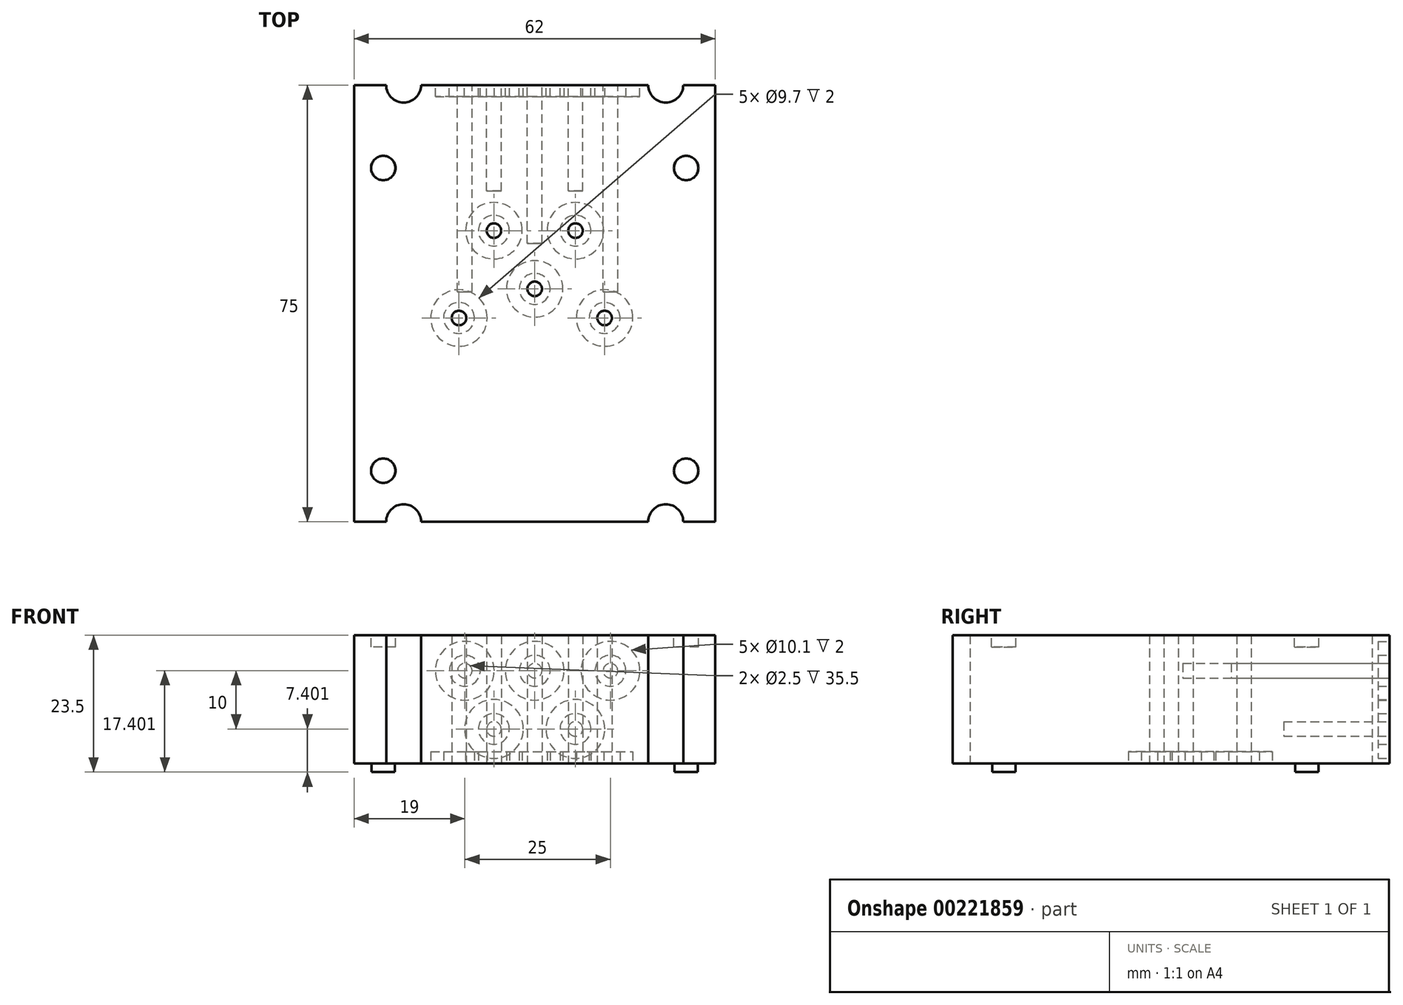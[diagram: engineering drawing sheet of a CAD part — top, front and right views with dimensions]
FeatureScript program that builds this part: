
annotation { "Feature Type Name" : "Feature", "Feature Type Description" : "" }
export const myFeature = defineFeature(function(context is Context, id is Id, definition is map)
    precondition{}
    {
        {
            var Q0;
            Q0=qCreatedBy(makeId("Top.planeOp"),FACE);
            var sketch = newSketch(context, id + "F0", { "sketchPlane" : qUnion([Q0])});
            skLineSegment(sketch, "E0.bottom", {"start": v(-31, 37.5) * mm, "end": v(31, 37.5) * mm});
            skLineSegment(sketch, "E0.top", {"start": v(-31, -37.5) * mm, "end": v(31, -37.5) * mm});
            skLineSegment(sketch, "E0.left", {"start": v(-31, 37.5) * mm, "end": v(-31, -37.5) * mm});
            skLineSegment(sketch, "E0.right", {"start": v(31, 37.5) * mm, "end": v(31, -37.5) * mm});
            skPoint(sketch, "E0.middle", {"position": v(0, 0) * mm});
            skSolve(sketch);
        }
        {
            var Q0;
            Q0=makeQuery(id+"F0.imprint","IMPRINT",FACE,{"disambiguationData":[TD([[makeQuery(id+"F0.imprint","IMPRINT",EDGE,{"derivedFrom":sQuery(id+"F0.wireOp",EDGE,"E0.bottom")}),-1.0]])]});
            extrude(context, id + "F1", {"entities" : qUnion([Q0]), "depth" : 14 * mm});
        }
        {
            var Q0;
            Q0=makeQuery(id+"F1.opExtrude","CAP_FACE",FACE,{"disambiguationData":[OSD([sQuery(id+"F0.wireOp",EDGE,"E0.bottom"),sQuery(id+"F0.wireOp",EDGE,"E0.top"),sQuery(id+"F0.wireOp",EDGE,"E0.left"),sQuery(id+"F0.wireOp",EDGE,"E0.right")])],"isStart":true});
            var sketch = newSketch(context, id + "F2", { "sketchPlane" : qUnion([Q0])});
            skLineSegment(sketch, "E1.bottom", {"start": v(-31, 37.5) * mm, "end": v(31, 37.5) * mm});
            skLineSegment(sketch, "E1.top", {"start": v(-31, -37.5) * mm, "end": v(31, -37.5) * mm});
            skLineSegment(sketch, "E1.left", {"start": v(-31, 37.5) * mm, "end": v(-31, -37.5) * mm});
            skLineSegment(sketch, "E1.right", {"start": v(31, 37.5) * mm, "end": v(31, -37.5) * mm});
            skPoint(sketch, "E1.middle", {"position": v(0, 0) * mm});
            skSolve(sketch);
        }
        {
            var Q0;
            Q0=qSketchRegion(id+"F2",true);
            extrude(context, id + "F3", {"entities" : qUnion([Q0]), "operationType" : NewBodyOperationType.ADD, "depth" : 8 * mm});
        }
        {
            var Q0;
            Q0=makeQuery(id+"F3.opExtrude","CAP_FACE",FACE,{"disambiguationData":[OSD([sQuery(id+"F2.wireOp",EDGE,"E1.bottom"),sQuery(id+"F2.wireOp",EDGE,"E1.top"),sQuery(id+"F2.wireOp",EDGE,"E1.left"),sQuery(id+"F2.wireOp",EDGE,"E1.right")])],"isStart":false});
            var sketch = newSketch(context, id + "F4", { "sketchPlane" : qUnion([Q0])});
            skCircle(sketch, "E2", {"center": v(-13, 2.5) * mm, "radius": 1.25 * mm});
            skCircle(sketch, "E3", {"center": v(-7, -12.5) * mm, "radius": 1.25 * mm});
            skCircle(sketch, "E4", {"center": v(12, 2.5) * mm, "radius": 1.25 * mm});
            skCircle(sketch, "E5", {"center": v(7, -12.5) * mm, "radius": 1.25 * mm});
            skCircle(sketch, "E6", {"center": v(0, -2.5) * mm, "radius": 1.25 * mm});
            skSolve(sketch);
        }
        {
            var Q0;
            Q0=makeQuery(id+"F4.imprint","IMPRINT",FACE,{"disambiguationData":[TD([[makeQuery(id+"F4.imprint","IMPRINT",EDGE,{"derivedFrom":sQuery(id+"F4.wireOp",EDGE,"E2")}),1.0]])]});
            var Q1;
            Q1=makeQuery(id+"F4.imprint","IMPRINT",FACE,{"disambiguationData":[TD([[makeQuery(id+"F4.imprint","IMPRINT",EDGE,{"derivedFrom":sQuery(id+"F4.wireOp",EDGE,"E3")}),1.0]])]});
            var Q2;
            Q2=makeQuery(id+"F4.imprint","IMPRINT",FACE,{"disambiguationData":[TD([[makeQuery(id+"F4.imprint","IMPRINT",EDGE,{"derivedFrom":sQuery(id+"F4.wireOp",EDGE,"E6")}),1.0]])]});
            var Q3;
            Q3=makeQuery(id+"F4.imprint","IMPRINT",FACE,{"disambiguationData":[TD([[makeQuery(id+"F4.imprint","IMPRINT",EDGE,{"derivedFrom":sQuery(id+"F4.wireOp",EDGE,"E5")}),1.0]])]});
            var Q4;
            Q4=makeQuery(id+"F4.imprint","IMPRINT",FACE,{"disambiguationData":[TD([[makeQuery(id+"F4.imprint","IMPRINT",EDGE,{"derivedFrom":sQuery(id+"F4.wireOp",EDGE,"E4")}),1.0]])]});
            extrude(context, id + "F5", {"entities" : qUnion([Q0, Q1, Q2, Q3, Q4]), "operationType" : NewBodyOperationType.REMOVE, "oppositeDirection" : true, "depth" : 38 * mm});
        }
        {
            var Q0;
            Q0=makeQuery(id+"F3.opExtrude","CAP_FACE",FACE,{"disambiguationData":[OSD([sQuery(id+"F2.wireOp",EDGE,"E1.bottom"),sQuery(id+"F2.wireOp",EDGE,"E1.top"),sQuery(id+"F2.wireOp",EDGE,"E1.left"),sQuery(id+"F2.wireOp",EDGE,"E1.right")])],"isStart":false});
            var sketch = newSketch(context, id + "F6", { "sketchPlane" : qUnion([Q0])});
            skCircle(sketch, "E7", {"center": v(-7, -12.5) * mm, "radius": 2.65 * mm});
            skCircle(sketch, "E8", {"center": v(-7, -12.5) * mm, "radius": 4.85 * mm});
            skCircle(sketch, "E9", {"center": v(-13, 2.5) * mm, "radius": 2.65 * mm});
            skCircle(sketch, "E10", {"center": v(-13, 2.5) * mm, "radius": 4.85 * mm});
            skCircle(sketch, "E11", {"center": v(0, -2.5) * mm, "radius": 2.65 * mm});
            skCircle(sketch, "E12", {"center": v(0, -2.5) * mm, "radius": 4.85 * mm});
            skCircle(sketch, "E13", {"center": v(12, 2.5) * mm, "radius": 2.65 * mm});
            skCircle(sketch, "E14", {"center": v(12, 2.5) * mm, "radius": 4.85 * mm});
            skCircle(sketch, "E15", {"center": v(7, -12.5) * mm, "radius": 2.65 * mm});
            skCircle(sketch, "E16", {"center": v(7, -12.5) * mm, "radius": 4.85 * mm});
            skSolve(sketch);
        }
        {
            var Q0;
            Q0=makeQuery(id+"F6.imprint","IMPRINT",FACE,{"disambiguationData":[TD([[makeQuery(id+"F6.imprint","IMPRINT",EDGE,{"derivedFrom":sQuery(id+"F6.wireOp",EDGE,"E7")}),-1.0]])]});
            var Q1;
            Q1=makeQuery(id+"F6.imprint","IMPRINT",FACE,{"disambiguationData":[TD([[makeQuery(id+"F6.imprint","IMPRINT",EDGE,{"derivedFrom":sQuery(id+"F6.wireOp",EDGE,"E9")}),-1.0]])]});
            var Q2;
            Q2=makeQuery(id+"F6.imprint","IMPRINT",FACE,{"disambiguationData":[TD([[makeQuery(id+"F6.imprint","IMPRINT",EDGE,{"derivedFrom":sQuery(id+"F6.wireOp",EDGE,"E11")}),-1.0]])]});
            var Q3;
            Q3=makeQuery(id+"F6.imprint","IMPRINT",FACE,{"disambiguationData":[TD([[makeQuery(id+"F6.imprint","IMPRINT",EDGE,{"derivedFrom":sQuery(id+"F6.wireOp",EDGE,"E13")}),-1.0]])]});
            var Q4;
            Q4=makeQuery(id+"F6.imprint","IMPRINT",FACE,{"disambiguationData":[TD([[makeQuery(id+"F6.imprint","IMPRINT",EDGE,{"derivedFrom":sQuery(id+"F6.wireOp",EDGE,"E15")}),-1.0]])]});
            extrude(context, id + "F7", {"entities" : qUnion([Q0, Q1, Q2, Q3, Q4]), "operationType" : NewBodyOperationType.REMOVE, "oppositeDirection" : true, "depth" : 2 * mm});
        }
        {
            var Q0;
            Q0=makeQuery(id+"F1.opExtrude","CAP_FACE",FACE,{"disambiguationData":[OSD([sQuery(id+"F0.wireOp",EDGE,"E0.bottom"),sQuery(id+"F0.wireOp",EDGE,"E0.top"),sQuery(id+"F0.wireOp",EDGE,"E0.left"),sQuery(id+"F0.wireOp",EDGE,"E0.right")])],"isStart":false});
            var sketch = newSketch(context, id + "F8", { "sketchPlane" : qUnion([Q0])});
            skCircle(sketch, "E17", {"center": v(-26, 23.26) * mm, "radius": 2.1 * mm});
            skCircle(sketch, "E18", {"center": v(-26, -28.74) * mm, "radius": 2.1 * mm});
            skCircle(sketch, "E19", {"center": v(26, -28.74) * mm, "radius": 2.1 * mm});
            skCircle(sketch, "E20", {"center": v(26, 23.26) * mm, "radius": 2.1 * mm});
            skSolve(sketch);
        }
        {
            var Q0;
            Q0=makeQuery(id+"F8.imprint","IMPRINT",FACE,{"disambiguationData":[TD([[makeQuery(id+"F8.imprint","IMPRINT",EDGE,{"derivedFrom":sQuery(id+"F8.wireOp",EDGE,"E17")}),1.0]])]});
            var Q1;
            Q1=makeQuery(id+"F8.imprint","IMPRINT",FACE,{"disambiguationData":[TD([[makeQuery(id+"F8.imprint","IMPRINT",EDGE,{"derivedFrom":sQuery(id+"F8.wireOp",EDGE,"E20")}),1.0]])]});
            var Q2;
            Q2=makeQuery(id+"F8.imprint","IMPRINT",FACE,{"disambiguationData":[TD([[makeQuery(id+"F8.imprint","IMPRINT",EDGE,{"derivedFrom":sQuery(id+"F8.wireOp",EDGE,"E19")}),1.0]])]});
            var Q3;
            Q3=makeQuery(id+"F8.imprint","IMPRINT",FACE,{"disambiguationData":[TD([[makeQuery(id+"F8.imprint","IMPRINT",EDGE,{"derivedFrom":sQuery(id+"F8.wireOp",EDGE,"E18")}),1.0]])]});
            extrude(context, id + "F9", {"entities" : qUnion([Q0, Q1, Q2, Q3]), "operationType" : NewBodyOperationType.REMOVE, "oppositeDirection" : true, "depth" : 2 * mm});
        }
        {
            var Q0;
            Q0=makeQuery(id+"F3.boolean.opBoolean","MERGE",FACE,{"derivedFrom":[makeQuery(id+"F1.opExtrude","SWEPT_FACE",FACE,{"disambiguationData":[OSD([sQuery(id+"F0.wireOp",EDGE,"E0.bottom")])]}),makeQuery(id+"F3.opExtrude","SWEPT_FACE",FACE,{"disambiguationData":[OSD([sQuery(id+"F2.wireOp",EDGE,"E1.top")])]})]});
            var sketch = newSketch(context, id + "F10", { "sketchPlane" : qUnion([Q0])});
            skCircle(sketch, "E21", {"center": v(7, -2.1) * mm, "radius": 1.25 * mm});
            skCircle(sketch, "E22", {"center": v(-13, 7.9) * mm, "radius": 1.25 * mm});
            skCircle(sketch, "E23", {"center": v(0, 7.9) * mm, "radius": 1.25 * mm});
            skCircle(sketch, "E24", {"center": v(12, 7.9) * mm, "radius": 1.25 * mm});
            skCircle(sketch, "E25", {"center": v(-7, -2.1) * mm, "radius": 1.25 * mm});
            skSolve(sketch);
        }
        {
            var Q0;
            Q0=makeQuery(id+"F10.imprint","IMPRINT",FACE,{"disambiguationData":[TD([[makeQuery(id+"F10.imprint","IMPRINT",EDGE,{"derivedFrom":sQuery(id+"F10.wireOp",EDGE,"E24")}),1.0]])]});
            var Q1;
            Q1=makeQuery(id+"F10.imprint","IMPRINT",FACE,{"disambiguationData":[TD([[makeQuery(id+"F10.imprint","IMPRINT",EDGE,{"derivedFrom":sQuery(id+"F10.wireOp",EDGE,"E22")}),1.0]])]});
            extrude(context, id + "F11", {"entities" : qUnion([Q0, Q1]), "operationType" : NewBodyOperationType.REMOVE, "oppositeDirection" : true, "depth" : 35.5 * mm});
        }
        {
            var Q0;
            Q0=makeQuery(id+"F3.boolean.opBoolean","MERGE",FACE,{"derivedFrom":[makeQuery(id+"F1.opExtrude","SWEPT_FACE",FACE,{"disambiguationData":[OSD([sQuery(id+"F0.wireOp",EDGE,"E0.bottom")])]}),makeQuery(id+"F3.opExtrude","SWEPT_FACE",FACE,{"disambiguationData":[OSD([sQuery(id+"F2.wireOp",EDGE,"E1.top")])]})]});
            var sketch = newSketch(context, id + "F12", { "sketchPlane" : qUnion([Q0])});
            skCircle(sketch, "E26", {"center": v(-13, 7.9) * mm, "radius": 5.05 * mm});
            skCircle(sketch, "E27", {"center": v(-7, -2.1) * mm, "radius": 5.05 * mm});
            skCircle(sketch, "E28", {"center": v(0, 7.9) * mm, "radius": 5.05 * mm});
            skCircle(sketch, "E29", {"center": v(7, -2.1) * mm, "radius": 5.05 * mm});
            skCircle(sketch, "E30", {"center": v(12, 7.9) * mm, "radius": 5.05 * mm});
            skCircle(sketch, "E31", {"center": v(-13, 7.9) * mm, "radius": 2.65 * mm});
            skCircle(sketch, "E32", {"center": v(-7, -2.1) * mm, "radius": 2.65 * mm});
            skCircle(sketch, "E33", {"center": v(0, 7.9) * mm, "radius": 2.65 * mm});
            skCircle(sketch, "E34", {"center": v(7, -2.1) * mm, "radius": 2.65 * mm});
            skCircle(sketch, "E35", {"center": v(12, 7.9) * mm, "radius": 2.65 * mm});
            skSolve(sketch);
        }
        {
            var Q0;
            Q0=makeQuery(id+"F12.imprint","IMPRINT",FACE,{"disambiguationData":[TD([[makeQuery(id+"F12.imprint","IMPRINT",EDGE,{"derivedFrom":sQuery(id+"F12.wireOp",EDGE,"E26")}),1.0]])]});
            var Q1;
            Q1=makeQuery(id+"F12.imprint","IMPRINT",FACE,{"disambiguationData":[TD([[makeQuery(id+"F12.imprint","IMPRINT",EDGE,{"derivedFrom":sQuery(id+"F12.wireOp",EDGE,"E27")}),1.0]])]});
            var Q2;
            Q2=makeQuery(id+"F12.imprint","IMPRINT",FACE,{"disambiguationData":[TD([[makeQuery(id+"F12.imprint","IMPRINT",EDGE,{"derivedFrom":sQuery(id+"F12.wireOp",EDGE,"E28")}),1.0]])]});
            var Q3;
            Q3=makeQuery(id+"F12.imprint","IMPRINT",FACE,{"disambiguationData":[TD([[makeQuery(id+"F12.imprint","IMPRINT",EDGE,{"derivedFrom":sQuery(id+"F12.wireOp",EDGE,"E29")}),1.0]])]});
            var Q4;
            Q4=makeQuery(id+"F12.imprint","IMPRINT",FACE,{"disambiguationData":[TD([[makeQuery(id+"F12.imprint","IMPRINT",EDGE,{"derivedFrom":sQuery(id+"F12.wireOp",EDGE,"E30")}),1.0]])]});
            extrude(context, id + "F13", {"entities" : qUnion([Q0, Q1, Q2, Q3, Q4]), "operationType" : NewBodyOperationType.REMOVE, "oppositeDirection" : true, "depth" : 2 * mm});
        }
        {
            var Q0;
            Q0=makeQuery(id+"F10.imprint","IMPRINT",FACE,{"disambiguationData":[TD([[makeQuery(id+"F10.imprint","IMPRINT",EDGE,{"derivedFrom":sQuery(id+"F10.wireOp",EDGE,"E23")}),1.0]])]});
            extrude(context, id + "F14", {"entities" : qUnion([Q0]), "operationType" : NewBodyOperationType.REMOVE, "oppositeDirection" : true, "depth" : 27.2 * mm});
        }
        {
            var Q0;
            Q0=makeQuery(id+"F10.imprint","IMPRINT",FACE,{"disambiguationData":[TD([[makeQuery(id+"F10.imprint","IMPRINT",EDGE,{"derivedFrom":sQuery(id+"F10.wireOp",EDGE,"E21")}),1.0]])]});
            var Q1;
            Q1=makeQuery(id+"F10.imprint","IMPRINT",FACE,{"disambiguationData":[TD([[makeQuery(id+"F10.imprint","IMPRINT",EDGE,{"derivedFrom":sQuery(id+"F10.wireOp",EDGE,"E25")}),1.0]])]});
            extrude(context, id + "F15", {"entities" : qUnion([Q0, Q1]), "operationType" : NewBodyOperationType.REMOVE, "oppositeDirection" : true, "depth" : 18.2 * mm});
        }
        {
            var Q0;
            {var subQ0=sQuery(id+"F2.wireOp",EDGE,"E1.right");var subQ1=sQuery(id+"F2.wireOp",EDGE,"E1.left");var subQ2=sQuery(id+"F2.wireOp",EDGE,"E1.top");var subQ3=sQuery(id+"F2.wireOp",EDGE,"E1.bottom");Q0=makeQuery(id+"F7.boolean.opBoolean","SPLIT",FACE,{"disambiguationData":[TD([makeQuery(id+"F1.opExtrude","SWEPT_FACE",FACE,{"disambiguationData":[OSD([sQuery(id+"F0.wireOp",EDGE,"E0.bottom")])]})])],"derivedFrom":makeQuery(id+"F3.opExtrude","CAP_FACE",FACE,{"disambiguationData":[OSD([subQ3,subQ2,subQ1,subQ0])],"isStart":false})});}
            var sketch = newSketch(context, id + "F16", { "sketchPlane" : qUnion([Q0])});
            skCircle(sketch, "E36", {"center": v(-22.5, 37.5) * mm, "radius": 3 * mm});
            skCircle(sketch, "E37", {"center": v(22.5, 37.5) * mm, "radius": 3 * mm});
            skCircle(sketch, "E38", {"center": v(22.5, -37.5) * mm, "radius": 3 * mm});
            skCircle(sketch, "E39", {"center": v(-22.5, -37.5) * mm, "radius": 3 * mm});
            skSolve(sketch);
        }
        {
            var Q0;
            {var subQ0=sQuery(id+"F16.wireOp",EDGE,"E36");var subQ1=makeQuery(id+"F3.opExtrude","CAP_EDGE",EDGE,{"disambiguationData":[OSD([sQuery(id+"F2.wireOp",EDGE,"E1.bottom")])],"isStart":false});var subQ2=makeQuery(id+"F16.imprint","INTERSECT",VERTEX,{"disambiguationData":[OD(0.0)],"derivedFrom":[subQ1,subQ0]});Q0=makeQuery(id+"F16.imprint","IMPRINT",FACE,{"disambiguationData":[TD([[makeQuery(id+"F16.imprint","IMPRINT",EDGE,{"disambiguationData":[TD([[subQ2,-1.0]])],"derivedFrom":subQ0}),1.0]])]});}
            var Q1;
            {var subQ0=sQuery(id+"F16.wireOp",EDGE,"E37");var subQ1=makeQuery(id+"F3.opExtrude","CAP_EDGE",EDGE,{"disambiguationData":[OSD([sQuery(id+"F2.wireOp",EDGE,"E1.bottom")])],"isStart":false});var subQ2=makeQuery(id+"F16.imprint","INTERSECT",VERTEX,{"disambiguationData":[OD(0.0)],"derivedFrom":[subQ1,subQ0]});Q1=makeQuery(id+"F16.imprint","IMPRINT",FACE,{"disambiguationData":[TD([[makeQuery(id+"F16.imprint","IMPRINT",EDGE,{"disambiguationData":[TD([[subQ2,1.0]])],"derivedFrom":subQ0}),1.0]])]});}
            var Q2;
            {var subQ0=sQuery(id+"F16.wireOp",EDGE,"E39");var subQ1=makeQuery(id+"F3.opExtrude","CAP_EDGE",EDGE,{"disambiguationData":[OSD([sQuery(id+"F2.wireOp",EDGE,"E1.top")])],"isStart":false});var subQ2=makeQuery(id+"F16.imprint","INTERSECT",VERTEX,{"disambiguationData":[OD(0.0)],"derivedFrom":[subQ1,subQ0]});Q2=makeQuery(id+"F16.imprint","IMPRINT",FACE,{"disambiguationData":[TD([[makeQuery(id+"F16.imprint","IMPRINT",EDGE,{"disambiguationData":[TD([[subQ2,1.0]])],"derivedFrom":subQ0}),1.0]])]});}
            var Q3;
            {var subQ0=sQuery(id+"F16.wireOp",EDGE,"E38");var subQ1=makeQuery(id+"F3.opExtrude","CAP_EDGE",EDGE,{"disambiguationData":[OSD([sQuery(id+"F2.wireOp",EDGE,"E1.top")])],"isStart":false});var subQ2=makeQuery(id+"F16.imprint","INTERSECT",VERTEX,{"disambiguationData":[OD(0.0)],"derivedFrom":[subQ1,subQ0]});Q3=makeQuery(id+"F16.imprint","IMPRINT",FACE,{"disambiguationData":[TD([[makeQuery(id+"F16.imprint","IMPRINT",EDGE,{"disambiguationData":[TD([[subQ2,-1.0]])],"derivedFrom":subQ0}),1.0]])]});}
            extrude(context, id + "F17", {"entities" : qUnion([Q0, Q1, Q2, Q3]), "operationType" : NewBodyOperationType.REMOVE, "oppositeDirection" : true, "depth" : 25 * mm});
        }
        {
            var Q0;
            {var subQ0=sQuery(id+"F2.wireOp",EDGE,"E1.right");var subQ1=sQuery(id+"F2.wireOp",EDGE,"E1.left");var subQ2=sQuery(id+"F2.wireOp",EDGE,"E1.top");var subQ3=sQuery(id+"F2.wireOp",EDGE,"E1.bottom");Q0=makeQuery(id+"F7.boolean.opBoolean","SPLIT",FACE,{"disambiguationData":[TD([makeQuery(id+"F1.opExtrude","SWEPT_FACE",FACE,{"disambiguationData":[OSD([sQuery(id+"F0.wireOp",EDGE,"E0.bottom")])]})])],"derivedFrom":makeQuery(id+"F3.opExtrude","CAP_FACE",FACE,{"disambiguationData":[OSD([subQ3,subQ2,subQ1,subQ0])],"isStart":false})});}
            var sketch = newSketch(context, id + "F18", { "sketchPlane" : qUnion([Q0])});
            skCircle(sketch, "E40", {"center": v(-26, 28.74) * mm, "radius": 2 * mm});
            skCircle(sketch, "E41", {"center": v(26, 28.74) * mm, "radius": 2 * mm});
            skCircle(sketch, "E42", {"center": v(26, -23.26) * mm, "radius": 2 * mm});
            skCircle(sketch, "E43", {"center": v(-26, -23.26) * mm, "radius": 2 * mm});
            skSolve(sketch);
        }
        {
            var Q0;
            Q0=makeQuery(id+"F18.imprint","IMPRINT",FACE,{"disambiguationData":[TD([[makeQuery(id+"F18.imprint","IMPRINT",EDGE,{"derivedFrom":sQuery(id+"F18.wireOp",EDGE,"E40")}),1.0]])]});
            var Q1;
            Q1=makeQuery(id+"F18.imprint","IMPRINT",FACE,{"disambiguationData":[TD([[makeQuery(id+"F18.imprint","IMPRINT",EDGE,{"derivedFrom":sQuery(id+"F18.wireOp",EDGE,"E41")}),1.0]])]});
            var Q2;
            Q2=makeQuery(id+"F18.imprint","IMPRINT",FACE,{"disambiguationData":[TD([[makeQuery(id+"F18.imprint","IMPRINT",EDGE,{"derivedFrom":sQuery(id+"F18.wireOp",EDGE,"E42")}),1.0]])]});
            var Q3;
            Q3=makeQuery(id+"F18.imprint","IMPRINT",FACE,{"disambiguationData":[TD([[makeQuery(id+"F18.imprint","IMPRINT",EDGE,{"derivedFrom":sQuery(id+"F18.wireOp",EDGE,"E43")}),1.0]])]});
            extrude(context, id + "F19", {"entities" : qUnion([Q0, Q1, Q2, Q3]), "operationType" : NewBodyOperationType.ADD, "depth" : 1.5 * mm});
        }
    });
